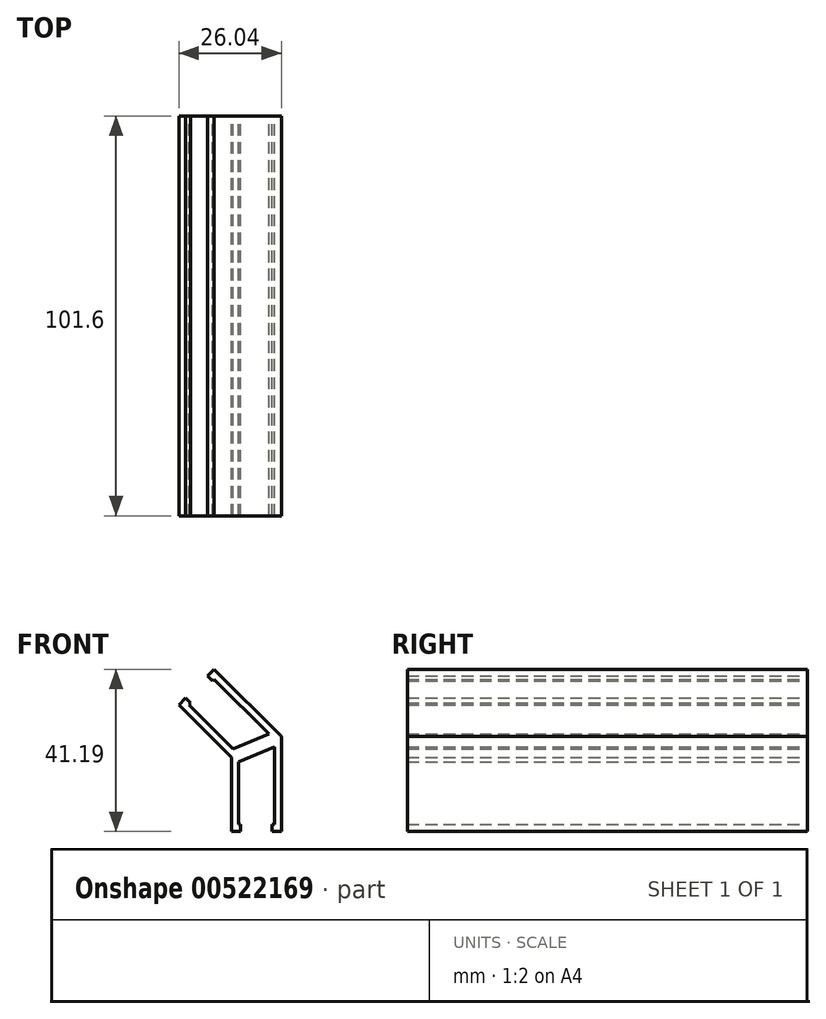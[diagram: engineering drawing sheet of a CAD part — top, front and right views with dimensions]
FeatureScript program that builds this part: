
annotation { "Feature Type Name" : "Feature", "Feature Type Description" : "" }
export const myFeature = defineFeature(function(context is Context, id is Id, definition is map)
    precondition{}
    {
        {
            var Q0;
            Q0=qCreatedBy(makeId("Front.planeOp"),FACE);
            var sketch = newSketch(context, id + "F0", { "sketchPlane" : qUnion([Q0])});
            skLineSegment(sketch, "E0", {"start": v(0, 0) * mm, "end": v(0, 24.13) * mm});
            skLineSegment(sketch, "E1", {"start": v(0, 0) * mm, "end": v(-2.36, 0) * mm});
            skLineSegment(sketch, "E2", {"start": v(-2.36, 0) * mm, "end": v(-2.36, 1.78) * mm});
            skLineSegment(sketch, "E3", {"start": v(-2.36, 1.78) * mm, "end": v(-1.78, 1.78) * mm});
            skLineSegment(sketch, "E4", {"start": v(-1.78, 1.78) * mm, "end": v(-1.78, 21.47) * mm});
            skLineSegment(sketch, "E5", {"start": v(0, 24.13) * mm, "end": v(-17.06, 41.2) * mm});
            skLineSegment(sketch, "E6", {"start": v(-17.06, 41.2) * mm, "end": v(-18.73, 39.52) * mm});
            skLineSegment(sketch, "E7", {"start": v(-18.73, 39.52) * mm, "end": v(-17.48, 38.26) * mm});
            skLineSegment(sketch, "E8", {"start": v(-17.48, 38.26) * mm, "end": v(-17.06, 38.68) * mm});
            skLineSegment(sketch, "E9", {"start": v(-17.06, 38.68) * mm, "end": v(-3.14, 24.75) * mm});
            skLineSegment(sketch, "E10", {"start": v(-10.34, 0) * mm, "end": v(-12.7, 0) * mm});
            skLineSegment(sketch, "E11", {"start": v(-12.7, 0) * mm, "end": v(-12.7, 18.87) * mm});
            skLineSegment(sketch, "E12", {"start": v(0, 24.13) * mm, "end": v(-12.7, 18.87) * mm, "construction": true});
            skLineSegment(sketch, "E13", {"start": v(-12.7, 18.87) * mm, "end": v(-26.04, 32.21) * mm});
            skLineSegment(sketch, "E14", {"start": v(-26.04, 32.21) * mm, "end": v(-24.37, 33.88) * mm});
            skLineSegment(sketch, "E15", {"start": v(-24.37, 33.88) * mm, "end": v(-23.12, 32.63) * mm});
            skLineSegment(sketch, "E16", {"start": v(-23.12, 32.63) * mm, "end": v(-23.53, 32.21) * mm});
            skLineSegment(sketch, "E17", {"start": v(-23.53, 32.21) * mm, "end": v(-12.28, 20.97) * mm});
            skLineSegment(sketch, "E18", {"start": v(-10.92, 17.68) * mm, "end": v(-10.92, 1.78) * mm});
            skLineSegment(sketch, "E19", {"start": v(-10.92, 1.78) * mm, "end": v(-10.34, 1.78) * mm});
            skLineSegment(sketch, "E20", {"start": v(-10.34, 1.78) * mm, "end": v(-10.34, 0) * mm});
            skLineSegment(sketch, "E21", {"start": v(-3.14, 24.75) * mm, "end": v(-12.28, 20.97) * mm});
            skLineSegment(sketch, "E22", {"start": v(-1.78, 21.47) * mm, "end": v(-10.92, 17.68) * mm});
            skSolve(sketch);
        }
        {
            var Q0;
            Q0 = qSketchRegion(id + "F0", true);
            extrude(context, id + "F1", {"entities" : qUnion([Q0]), "depth" : 101.6 * mm, "offsetDistance" : 25.4 * mm});
        }
    });
